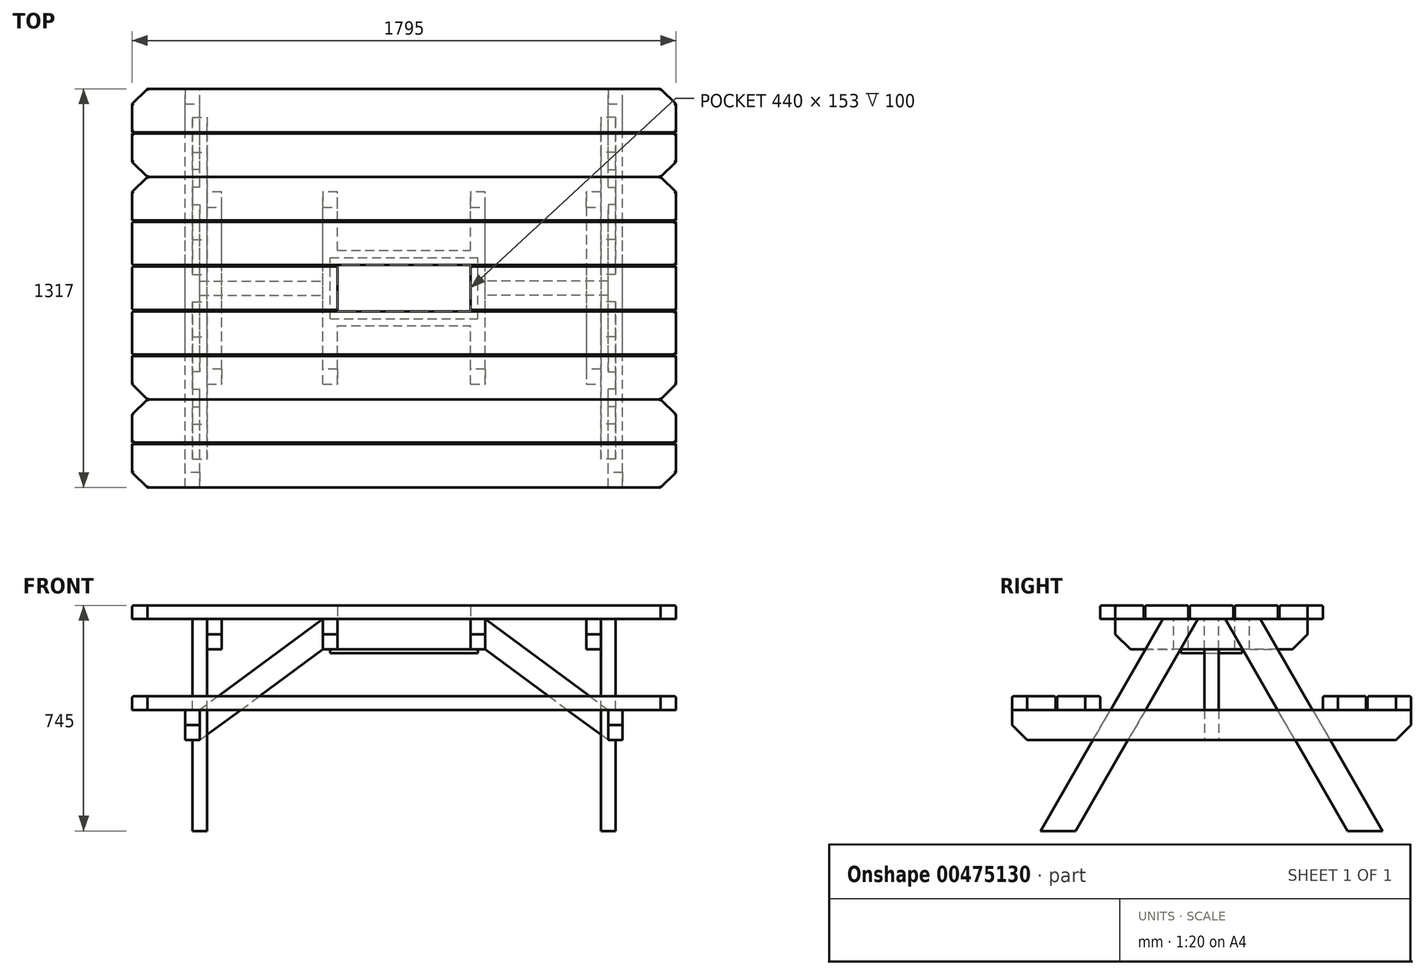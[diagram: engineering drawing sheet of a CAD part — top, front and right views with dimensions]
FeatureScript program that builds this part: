
annotation { "Feature Type Name" : "Feature", "Feature Type Description" : "" }
export const myFeature = defineFeature(function(context is Context, id is Id, definition is map)
    precondition{}
    {
        {
            var Q0;
            Q0=qCreatedBy(makeId("Top.planeOp"),FACE);
            var sketch = newSketch(context, id + "F0", { "sketchPlane" : qUnion([Q0])});
            skLineSegment(sketch, "E0.bottom", {"start": v(897.5, -71.5) * mm, "end": v(-897.5, -71.5) * mm});
            skLineSegment(sketch, "E0.top", {"start": v(897.5, 71.5) * mm, "end": v(-897.5, 71.5) * mm});
            skLineSegment(sketch, "E0.left", {"start": v(897.5, -71.5) * mm, "end": v(897.5, 71.5) * mm});
            skLineSegment(sketch, "E0.right", {"start": v(-897.5, -71.5) * mm, "end": v(-897.5, 71.5) * mm});
            skPoint(sketch, "E0.middle", {"position": v(0, 0) * mm});
            skLineSegment(sketch, "E1.bottom", {"start": v(-897.5, -76.5) * mm, "end": v(897.5, -76.5) * mm});
            skLineSegment(sketch, "E1.top", {"start": v(-897.5, -219.5) * mm, "end": v(897.5, -219.5) * mm});
            skLineSegment(sketch, "E1.left", {"start": v(-897.5, -76.5) * mm, "end": v(-897.5, -219.5) * mm});
            skLineSegment(sketch, "E1.right", {"start": v(897.5, -76.5) * mm, "end": v(897.5, -219.5) * mm});
            skLineSegment(sketch, "E2.bottom", {"start": v(-897.5, -224.5) * mm, "end": v(897.5, -224.5) * mm});
            skLineSegment(sketch, "E2.left", {"start": v(-897.5, -224.5) * mm, "end": v(-897.5, -367.5) * mm});
            skLineSegment(sketch, "E2.right", {"start": v(897.5, -224.5) * mm, "end": v(897.5, -367.5) * mm});
            skLineSegment(sketch, "E3.bottom", {"start": v(-897.5, 76.5) * mm, "end": v(897.5, 76.5) * mm});
            skLineSegment(sketch, "E3.top", {"start": v(-897.5, 219.5) * mm, "end": v(897.5, 219.5) * mm});
            skLineSegment(sketch, "E3.left", {"start": v(-897.5, 76.5) * mm, "end": v(-897.5, 219.5) * mm});
            skLineSegment(sketch, "E3.right", {"start": v(897.5, 76.5) * mm, "end": v(897.5, 219.5) * mm});
            skLineSegment(sketch, "E4.bottom", {"start": v(-897.5, 224.5) * mm, "end": v(897.5, 224.5) * mm});
            skLineSegment(sketch, "E4.top", {"start": v(-897.5, 367.5) * mm, "end": v(897.5, 367.5) * mm});
            skLineSegment(sketch, "E4.left", {"start": v(-897.5, 224.5) * mm, "end": v(-897.5, 367.5) * mm});
            skLineSegment(sketch, "E4.right", {"start": v(897.5, 224.5) * mm, "end": v(897.5, 367.5) * mm});
            skLineSegment(sketch, "E5.bottom", {"start": v(-897.5, -367.5) * mm, "end": v(897.5, -367.5) * mm});
            skSolve(sketch);
        }
        {
            var Q0;
            Q0 = qSketchRegion(id + "F0", true);
            extrude(context, id + "F1", {"entities" : qUnion([Q0]), "depth" : 45 * mm, "offsetDistance" : 25 * mm});
        }
        {
            var Q0;
            Q0=qCreatedBy(makeId("Right.planeOp"),FACE);
            cPlane(context, id + "F2", {"entities" : qUnion([Q0]), "cplaneType" : CPlaneType.OFFSET, "offset" : 650 * mm, "width" : 150 * mm, "height" : 150 * mm});
        }
        {
            var Q0;
            Q0=qCreatedBy(id+"F2.planeOp",FACE);
            var sketch = newSketch(context, id + "F3", { "sketchPlane" : qUnion([Q0])});
            skLineSegment(sketch, "E6", {"start": v(160.47, 0) * mm, "end": v(564.62, -700) * mm});
            skLineSegment(sketch, "E7", {"start": v(564.62, -700) * mm, "end": v(449.15, -700) * mm});
            skLineSegment(sketch, "E8", {"start": v(449.15, -700) * mm, "end": v(45, 0) * mm});
            skLineSegment(sketch, "E9", {"start": v(45, 0) * mm, "end": v(160.47, 0) * mm});
            skLineSegment(sketch, "E10", {"start": v(-45, 0) * mm, "end": v(-449.15, -700) * mm});
            skLineSegment(sketch, "E11", {"start": v(-449.15, -700) * mm, "end": v(-564.62, -700) * mm});
            skLineSegment(sketch, "E12", {"start": v(-564.62, -700) * mm, "end": v(-160.47, 0) * mm});
            skLineSegment(sketch, "E13", {"start": v(-160.47, 0) * mm, "end": v(-45, 0) * mm});
            skLineSegment(sketch, "E14", {"start": v(-449.15, -700) * mm, "end": v(-449.15, -593.82) * mm});
            skSolve(sketch);
        }
        {
            var Q0;
            Q0 = qSketchRegion(id + "F3", true);
            extrude(context, id + "F4", {"entities" : qUnion([Q0]), "depth" : 48 * mm, "offsetDistance" : 25 * mm});
        }
        {
            var Q0;
            Q0=makeQuery(id+"F4.opExtrude","CAP_FACE",FACE,{"disambiguationData":[OSD([sQuery(id+"F3.wireOp",EDGE,"E10"),sQuery(id+"F3.wireOp",EDGE,"E11"),sQuery(id+"F3.wireOp",EDGE,"E12"),sQuery(id+"F3.wireOp",EDGE,"E13")])],"isStart":false});
            var sketch = newSketch(context, id + "F5", { "sketchPlane" : qUnion([Q0])});
            skLineSegment(sketch, "E15.bottom", {"start": v(-658.5, -300) * mm, "end": v(658.5, -300) * mm});
            skLineSegment(sketch, "E15.top", {"start": v(-658.5, -400) * mm, "end": v(658.5, -400) * mm});
            skLineSegment(sketch, "E15.left", {"start": v(-658.5, -300) * mm, "end": v(-658.5, -400) * mm});
            skLineSegment(sketch, "E15.right", {"start": v(658.5, -300) * mm, "end": v(658.5, -400) * mm});
            skLineSegment(sketch, "E16", {"start": v(-658.5, -300) * mm, "end": v(-333.68, -300) * mm});
            skSolve(sketch);
        }
        {
            var Q0;
            Q0 = qSketchRegion(id + "F5", true);
            extrude(context, id + "F6", {"entities" : qUnion([Q0]), "operationType" : NewBodyOperationType.ADD, "depth" : 24 * mm, "offsetDistance" : 25 * mm, "hasSecondDirection" : true, "secondDirectionOppositeDirection" : true, "secondDirectionDepth" : 24 * mm});
        }
        {
            var Q0;
            Q0=makeQuery(id+"F4.opExtrude","SWEPT_BODY",BODY,{"disambiguationData":[OSD([sQuery(id+"F3.wireOp",EDGE,"E6"),sQuery(id+"F3.wireOp",EDGE,"E7"),sQuery(id+"F3.wireOp",EDGE,"E8"),sQuery(id+"F3.wireOp",EDGE,"E9")])]});
            var Q1;
            Q1=qCreatedBy(makeId("Right.planeOp"),FACE);
            mirror(context, id + "F7", {"entities" : qUnion([Q0]), "mirrorPlane" : qUnion([Q1])});
        }
        {
            var Q0;
            Q0=makeQuery(id+"F7.opPattern","COPY",FACE,{"derivedFrom":makeQuery(id+"F6.opExtrude","SWEPT_FACE",FACE,{"disambiguationData":[OSD([sQuery(id+"F5.wireOp",EDGE,"E15.bottom")])]}),"instanceName":"1"});
            var sketch = newSketch(context, id + "F8", { "sketchPlane" : qUnion([Q0])});
            skLineSegment(sketch, "E17.bottom", {"start": v(-897.5, -658.5) * mm, "end": v(897.5, -658.5) * mm});
            skLineSegment(sketch, "E17.top", {"start": v(-897.5, -515.5) * mm, "end": v(897.5, -515.5) * mm});
            skLineSegment(sketch, "E17.left", {"start": v(-897.5, -658.5) * mm, "end": v(-897.5, -515.5) * mm});
            skLineSegment(sketch, "E17.right", {"start": v(897.5, -658.5) * mm, "end": v(897.5, -515.5) * mm});
            skLineSegment(sketch, "E18.bottom", {"start": v(-897.5, -510.5) * mm, "end": v(897.5, -510.5) * mm});
            skLineSegment(sketch, "E18.top", {"start": v(-897.5, -367.5) * mm, "end": v(897.5, -367.5) * mm});
            skLineSegment(sketch, "E18.left", {"start": v(-897.5, -510.5) * mm, "end": v(-897.5, -367.5) * mm});
            skLineSegment(sketch, "E18.right", {"start": v(897.5, -510.5) * mm, "end": v(897.5, -367.5) * mm});
            skLineSegment(sketch, "E19.bottom", {"start": v(897.5, 367.5) * mm, "end": v(-897.5, 367.5) * mm});
            skLineSegment(sketch, "E19.top", {"start": v(897.5, 510.5) * mm, "end": v(-897.5, 510.5) * mm});
            skLineSegment(sketch, "E19.left", {"start": v(897.5, 367.5) * mm, "end": v(897.5, 510.5) * mm});
            skLineSegment(sketch, "E19.right", {"start": v(-897.5, 367.5) * mm, "end": v(-897.5, 510.5) * mm});
            skLineSegment(sketch, "E20.bottom", {"start": v(-897.5, 515.5) * mm, "end": v(897.5, 515.5) * mm});
            skLineSegment(sketch, "E20.top", {"start": v(-897.5, 658.5) * mm, "end": v(897.5, 658.5) * mm});
            skLineSegment(sketch, "E20.left", {"start": v(-897.5, 515.5) * mm, "end": v(-897.5, 658.5) * mm});
            skLineSegment(sketch, "E20.right", {"start": v(897.5, 515.5) * mm, "end": v(897.5, 658.5) * mm});
            skSolve(sketch);
        }
        {
            var Q0;
            Q0 = qSketchRegion(id + "F8", true);
            extrude(context, id + "F9", {"entities" : qUnion([Q0]), "depth" : 45 * mm, "offsetDistance" : 25 * mm});
        }
        {
            var Q0;
            Q0=makeQuery(id+"F6.opExtrude","CAP_FACE",FACE,{"disambiguationData":[OSD([sQuery(id+"F5.wireOp",EDGE,"E15.bottom"),sQuery(id+"F5.wireOp",EDGE,"E15.top"),sQuery(id+"F5.wireOp",EDGE,"E15.left"),sQuery(id+"F5.wireOp",EDGE,"E15.right")])],"isStart":false});
            var sketch = newSketch(context, id + "F10", { "sketchPlane" : qUnion([Q0])});
            skCircle(sketch, "E21", {"center": v(-431.43, -325) * mm, "radius": 5 * mm});
            skCircle(sketch, "E22", {"center": v(-405.45, -375) * mm, "radius": 5 * mm});
            skCircle(sketch, "E23", {"center": v(356.98, -325) * mm, "radius": 5 * mm});
            skCircle(sketch, "E24", {"center": v(474.1, -375) * mm, "radius": 5 * mm});
            skSolve(sketch);
        }
        {
            var Q0;
            Q0=makeQuery(id+"F1.opExtrude","CAP_FACE",FACE,{"disambiguationData":[OSD([sQuery(id+"F0.wireOp",EDGE,"E5.bottom"),sQuery(id+"F0.wireOp",EDGE,"E5.top"),sQuery(id+"F0.wireOp",EDGE,"E5.left"),sQuery(id+"F0.wireOp",EDGE,"E5.right")])],"isStart":true});
            var sketch = newSketch(context, id + "F11", { "sketchPlane" : qUnion([Q0])});
            skLineSegment(sketch, "E25.bottom", {"start": v(-650, 317.5) * mm, "end": v(-602, 317.5) * mm});
            skLineSegment(sketch, "E25.top", {"start": v(-650, -317.5) * mm, "end": v(-602, -317.5) * mm});
            skLineSegment(sketch, "E25.left", {"start": v(-650, 317.5) * mm, "end": v(-650, -317.5) * mm});
            skLineSegment(sketch, "E25.right", {"start": v(-602, 317.5) * mm, "end": v(-602, -317.5) * mm});
            skLineSegment(sketch, "E26.bottom", {"start": v(650, -317.5) * mm, "end": v(602, -317.5) * mm});
            skLineSegment(sketch, "E26.top", {"start": v(650, 317.5) * mm, "end": v(602, 317.5) * mm});
            skLineSegment(sketch, "E26.left", {"start": v(650, -317.5) * mm, "end": v(650, 317.5) * mm});
            skLineSegment(sketch, "E26.right", {"start": v(602, -317.5) * mm, "end": v(602, 317.5) * mm});
            skSolve(sketch);
        }
        {
            var Q0;
            Q0 = qSketchRegion(id + "F11", true);
            extrude(context, id + "F12", {"entities" : qUnion([Q0]), "depth" : 100 * mm, "offsetDistance" : 25 * mm});
        }
        {
            var Q0;
            {var subQ0=sQuery(id+"F3.wireOp",EDGE,"E10");var subQ1=sQuery(id+"F3.wireOp",EDGE,"E13");var subQ2=sQuery(id+"F3.wireOp",EDGE,"E12");Q0=makeQuery(id+"F6.boolean.opBoolean","SPLIT",FACE,{"disambiguationData":[TD([makeQuery(id+"F4.opExtrude","SWEPT_FACE",FACE,{"disambiguationData":[OSD([subQ1])]})])],"derivedFrom":makeQuery(id+"F4.opExtrude","CAP_FACE",FACE,{"disambiguationData":[OSD([subQ0,sQuery(id+"F3.wireOp",EDGE,"E11"),subQ2,subQ1])],"isStart":false})});}
            var sketch = newSketch(context, id + "F13", { "sketchPlane" : qUnion([Q0])});
            skCircle(sketch, "E27", {"center": v(-112.04, -24.63) * mm, "radius": 5 * mm});
            skCircle(sketch, "E28", {"center": v(-236.98, -84.16) * mm, "radius": 5 * mm});
            skCircle(sketch, "E29", {"center": v(97.88, -24.63) * mm, "radius": 5 * mm});
            skCircle(sketch, "E30", {"center": v(207.03, -84.16) * mm, "radius": 5 * mm});
            skSolve(sketch);
        }
        {
            var Q0;
            Q0=makeQuery(id+"F1.opExtrude","CAP_FACE",FACE,{"disambiguationData":[OSD([sQuery(id+"F0.wireOp",EDGE,"E1.bottom"),sQuery(id+"F0.wireOp",EDGE,"E1.top"),sQuery(id+"F0.wireOp",EDGE,"E1.left"),sQuery(id+"F0.wireOp",EDGE,"E1.right")])],"isStart":true});
            var sketch = newSketch(context, id + "F14", { "sketchPlane" : qUnion([Q0])});
            skLineSegment(sketch, "E31.bottom", {"start": v(-268, 317.5) * mm, "end": v(-220, 317.5) * mm});
            skLineSegment(sketch, "E31.top", {"start": v(-268, -317.5) * mm, "end": v(-220, -317.5) * mm});
            skLineSegment(sketch, "E31.left", {"start": v(-268, 317.5) * mm, "end": v(-268, -317.5) * mm});
            skLineSegment(sketch, "E31.right", {"start": v(-220, 317.5) * mm, "end": v(-220, -317.5) * mm});
            skLineSegment(sketch, "E32.bottom", {"start": v(220, 317.5) * mm, "end": v(268, 317.5) * mm});
            skLineSegment(sketch, "E32.top", {"start": v(220, -317.5) * mm, "end": v(268, -317.5) * mm});
            skLineSegment(sketch, "E32.left", {"start": v(220, 317.5) * mm, "end": v(220, -317.5) * mm});
            skLineSegment(sketch, "E32.right", {"start": v(268, 317.5) * mm, "end": v(268, -317.5) * mm});
            skLineSegment(sketch, "E33.bottom", {"start": v(-220, -76.5) * mm, "end": v(220, -76.5) * mm});
            skLineSegment(sketch, "E33.top", {"start": v(-220, -124.5) * mm, "end": v(220, -124.5) * mm});
            skLineSegment(sketch, "E33.left", {"start": v(-220, -76.5) * mm, "end": v(-220, -124.5) * mm});
            skLineSegment(sketch, "E33.right", {"start": v(220, -76.5) * mm, "end": v(220, -124.5) * mm});
            skLineSegment(sketch, "E34.left", {"start": v(-220, 124.5) * mm, "end": v(-220, 76.5) * mm});
            skLineSegment(sketch, "E34.right", {"start": v(220, 124.5) * mm, "end": v(220, 76.5) * mm});
            skLineSegment(sketch, "E35", {"start": v(-220, 76.5) * mm, "end": v(220, 76.5) * mm});
            skLineSegment(sketch, "E36", {"start": v(-220, 124.5) * mm, "end": v(220, 124.5) * mm});
            skSolve(sketch);
        }
        {
            var Q0;
            Q0 = qSketchRegion(id + "F14", true);
            extrude(context, id + "F15", {"entities" : qUnion([Q0]), "depth" : 100 * mm, "offsetDistance" : 25 * mm});
        }
        {
            var Q0;
            Q0=makeQuery(id+"F1.opExtrude","CAP_FACE",FACE,{"disambiguationData":[OSD([sQuery(id+"F0.wireOp",EDGE,"E1.bottom"),sQuery(id+"F0.wireOp",EDGE,"E1.top"),sQuery(id+"F0.wireOp",EDGE,"E1.left"),sQuery(id+"F0.wireOp",EDGE,"E1.right")])],"isStart":true});
            var sketch = newSketch(context, id + "F16", { "sketchPlane" : qUnion([Q0])});
            skLineSegment(sketch, "E37.bottom", {"start": v(220, 76.5) * mm, "end": v(-220, 76.5) * mm});
            skLineSegment(sketch, "E37.top", {"start": v(-220, -76.5) * mm, "end": v(220, -76.5) * mm});
            skLineSegment(sketch, "E37.left", {"start": v(-220, 76.5) * mm, "end": v(-220, -76.5) * mm});
            skLineSegment(sketch, "E37.right", {"start": v(220, 76.5) * mm, "end": v(220, -76.5) * mm});
            skSolve(sketch);
        }
        {
            var Q0;
            Q0 = qSketchRegion(id + "F16", true);
            extrude(context, id + "F17", {"entities" : qUnion([Q0]), "operationType" : NewBodyOperationType.REMOVE, "endBound" : BoundingType.THROUGH_ALL, "oppositeDirection" : true, "depth" : 25 * mm, "offsetDistance" : 25 * mm});
        }
        {
            var Q0;
            Q0=makeQuery(id+"F15.opExtrude","CAP_FACE",FACE,{"disambiguationData":[OSD([sQuery(id+"F14.wireOp",EDGE,"E31.bottom"),sQuery(id+"F14.wireOp",EDGE,"E31.top"),sQuery(id+"F14.wireOp",EDGE,"E31.left"),sQuery(id+"F14.wireOp",EDGE,"E31.right"),sQuery(id+"F14.wireOp",EDGE,"E32.bottom"),sQuery(id+"F14.wireOp",EDGE,"E32.top"),sQuery(id+"F14.wireOp",EDGE,"E32.left"),sQuery(id+"F14.wireOp",EDGE,"E32.right"),sQuery(id+"F14.wireOp",EDGE,"E33.bottom"),sQuery(id+"F14.wireOp",EDGE,"E33.top"),sQuery(id+"F14.wireOp",EDGE,"E35"),sQuery(id+"F14.wireOp",EDGE,"yrt6tq8n-YOMr-yxpr-mFNC-kb3xUqAydBUf")])],"isStart":false});
            var sketch = newSketch(context, id + "F18", { "sketchPlane" : qUnion([Q0])});
            skLineSegment(sketch, "E38.bottom", {"start": v(-244, 100.5) * mm, "end": v(244, 100.5) * mm});
            skLineSegment(sketch, "E38.top", {"start": v(-244, -100.5) * mm, "end": v(244, -100.5) * mm});
            skLineSegment(sketch, "E38.left", {"start": v(-244, 100.5) * mm, "end": v(-244, -100.5) * mm});
            skLineSegment(sketch, "E38.right", {"start": v(244, 100.5) * mm, "end": v(244, -100.5) * mm});
            skSolve(sketch);
        }
        {
            var Q0;
            Q0 = qSketchRegion(id + "F18", true);
            extrude(context, id + "F19", {"entities" : qUnion([Q0]), "operationType" : NewBodyOperationType.ADD, "depth" : 12.5 * mm, "offsetDistance" : 25 * mm});
        }
        {
            var Q0;
            Q0=qCreatedBy(makeId("Front.planeOp"),FACE);
            var sketch = newSketch(context, id + "F20", { "sketchPlane" : qUnion([Q0])});
            skLineSegment(sketch, "E39", {"start": v(-674, -400) * mm, "end": v(-268, -100) * mm});
            skLineSegment(sketch, "E40", {"start": v(-268, -100) * mm, "end": v(-268, 0) * mm});
            skLineSegment(sketch, "E41", {"start": v(-268, 0) * mm, "end": v(-674, -300) * mm});
            skLineSegment(sketch, "E42", {"start": v(-674, -300) * mm, "end": v(-674, -400) * mm});
            skSolve(sketch);
        }
        {
            var Q0;
            Q0 = qSketchRegion(id + "F20", true);
            extrude(context, id + "F21", {"entities" : qUnion([Q0]), "depth" : 24 * mm, "offsetDistance" : 25 * mm, "hasSecondDirection" : true, "secondDirectionOppositeDirection" : true, "secondDirectionDepth" : 24 * mm});
        }
        {
            var Q0;
            Q0=makeQuery(id+"F21.opExtrude","SWEPT_BODY",BODY,{"disambiguationData":[OSD([sQuery(id+"F20.wireOp",EDGE,"E39"),sQuery(id+"F20.wireOp",EDGE,"E40"),sQuery(id+"F20.wireOp",EDGE,"E41"),sQuery(id+"F20.wireOp",EDGE,"E42")])]});
            var Q1;
            Q1=qCreatedBy(makeId("Right.planeOp"),FACE);
            mirror(context, id + "F22", {"entities" : qUnion([Q0]), "mirrorPlane" : qUnion([Q1])});
        }
        {
            var Q0;
            Q0=makeQuery(id+"F9.opExtrude","SWEPT_EDGE",EDGE,{"disambiguationData":[OSD([sQuery(id+"F8.wireOp",EDGE,"E17.bottom"),sQuery(id+"F8.wireOp",EDGE,"E17.right")])]});
            var Q1;
            Q1=makeQuery(id+"F9.opExtrude","SWEPT_EDGE",EDGE,{"disambiguationData":[OSD([sQuery(id+"F8.wireOp",EDGE,"E20.top"),sQuery(id+"F8.wireOp",EDGE,"E20.right")])]});
            var Q2;
            Q2=makeQuery(id+"F9.opExtrude","SWEPT_EDGE",EDGE,{"disambiguationData":[OSD([sQuery(id+"F8.wireOp",EDGE,"E20.top"),sQuery(id+"F8.wireOp",EDGE,"E20.left")])]});
            var Q3;
            Q3=makeQuery(id+"F9.opExtrude","SWEPT_EDGE",EDGE,{"disambiguationData":[OSD([sQuery(id+"F8.wireOp",EDGE,"E17.bottom"),sQuery(id+"F8.wireOp",EDGE,"E17.left")])]});
            var Q4;
            Q4=makeQuery(id+"F7.opPattern","COPY",EDGE,{"derivedFrom":makeQuery(id+"F6.opExtrude","SWEPT_EDGE",EDGE,{"disambiguationData":[OSD([sQuery(id+"F5.wireOp",EDGE,"E15.top"),sQuery(id+"F5.wireOp",EDGE,"E15.left")])]}),"instanceName":"1"});
            var Q5;
            Q5=makeQuery(id+"F12.opExtrude","CAP_EDGE",EDGE,{"disambiguationData":[OSD([sQuery(id+"F11.wireOp",EDGE,"E25.top")])],"isStart":false});
            var Q6;
            Q6=makeQuery(id+"F15.opExtrude","CAP_EDGE",EDGE,{"disambiguationData":[OSD([sQuery(id+"F14.wireOp",EDGE,"E31.top")])],"isStart":false});
            var Q7;
            Q7=makeQuery(id+"F15.opExtrude","CAP_EDGE",EDGE,{"disambiguationData":[OSD([sQuery(id+"F14.wireOp",EDGE,"E32.top")])],"isStart":false});
            var Q8;
            Q8=makeQuery(id+"F12.opExtrude","CAP_EDGE",EDGE,{"disambiguationData":[OSD([sQuery(id+"F11.wireOp",EDGE,"E26.bottom")])],"isStart":false});
            var Q9;
            Q9=makeQuery(id+"F15.opExtrude","CAP_EDGE",EDGE,{"disambiguationData":[OSD([sQuery(id+"F14.wireOp",EDGE,"E31.bottom")])],"isStart":false});
            var Q10;
            Q10=makeQuery(id+"F12.opExtrude","CAP_EDGE",EDGE,{"disambiguationData":[OSD([sQuery(id+"F11.wireOp",EDGE,"E25.bottom")])],"isStart":false});
            var Q11;
            Q11=makeQuery(id+"F15.opExtrude","CAP_EDGE",EDGE,{"disambiguationData":[OSD([sQuery(id+"F14.wireOp",EDGE,"E32.bottom")])],"isStart":false});
            var Q12;
            Q12=makeQuery(id+"F12.opExtrude","CAP_EDGE",EDGE,{"disambiguationData":[OSD([sQuery(id+"F11.wireOp",EDGE,"E26.top")])],"isStart":false});
            var Q13;
            Q13=makeQuery(id+"F6.opExtrude","SWEPT_EDGE",EDGE,{"disambiguationData":[OSD([sQuery(id+"F5.wireOp",EDGE,"E15.top"),sQuery(id+"F5.wireOp",EDGE,"E15.left")])]});
            var Q14;
            Q14=makeQuery(id+"F7.opPattern","COPY",EDGE,{"derivedFrom":makeQuery(id+"F6.opExtrude","SWEPT_EDGE",EDGE,{"disambiguationData":[OSD([sQuery(id+"F5.wireOp",EDGE,"E15.top"),sQuery(id+"F5.wireOp",EDGE,"E15.right")])]}),"instanceName":"1"});
            var Q15;
            Q15=makeQuery(id+"F6.opExtrude","SWEPT_EDGE",EDGE,{"disambiguationData":[OSD([sQuery(id+"F5.wireOp",EDGE,"E15.top"),sQuery(id+"F5.wireOp",EDGE,"E15.right")])]});
            var Q16;
            Q16=makeQuery(id+"F1.opExtrude","SWEPT_EDGE",EDGE,{"disambiguationData":[OSD([sQuery(id+"F0.wireOp",EDGE,"E4.top"),sQuery(id+"F0.wireOp",EDGE,"E4.left")])]});
            var Q17;
            Q17=makeQuery(id+"F1.opExtrude","SWEPT_EDGE",EDGE,{"disambiguationData":[OSD([sQuery(id+"F0.wireOp",EDGE,"E2.left"),sQuery(id+"F0.wireOp",EDGE,"E5.bottom")])]});
            var Q18;
            Q18=makeQuery(id+"F1.opExtrude","SWEPT_EDGE",EDGE,{"disambiguationData":[OSD([sQuery(id+"F0.wireOp",EDGE,"E2.right"),sQuery(id+"F0.wireOp",EDGE,"E5.bottom")])]});
            var Q19;
            Q19=makeQuery(id+"F1.opExtrude","SWEPT_EDGE",EDGE,{"disambiguationData":[OSD([sQuery(id+"F0.wireOp",EDGE,"E4.top"),sQuery(id+"F0.wireOp",EDGE,"E4.right")])]});
            var Q20;
            Q20=makeQuery(id+"F9.opExtrude","SWEPT_EDGE",EDGE,{"disambiguationData":[OSD([sQuery(id+"F8.wireOp",EDGE,"E19.bottom"),sQuery(id+"F8.wireOp",EDGE,"E19.left")])]});
            var Q21;
            Q21=makeQuery(id+"F9.opExtrude","SWEPT_EDGE",EDGE,{"disambiguationData":[OSD([sQuery(id+"F8.wireOp",EDGE,"E18.top"),sQuery(id+"F8.wireOp",EDGE,"E18.right")])]});
            var Q22;
            Q22=makeQuery(id+"F9.opExtrude","SWEPT_EDGE",EDGE,{"disambiguationData":[OSD([sQuery(id+"F8.wireOp",EDGE,"E19.bottom"),sQuery(id+"F8.wireOp",EDGE,"E19.right")])]});
            var Q23;
            Q23=makeQuery(id+"F9.opExtrude","SWEPT_EDGE",EDGE,{"disambiguationData":[OSD([sQuery(id+"F8.wireOp",EDGE,"E18.top"),sQuery(id+"F8.wireOp",EDGE,"E18.left")])]});
            chamfer(context, id + "F23", {"entities" : qUnion([Q0, Q1, Q2, Q3, Q4, Q5, Q6, Q7, Q8, Q9, Q10, Q11, Q12, Q13, Q14, Q15, Q16, Q17, Q18, Q19, Q20, Q21, Q22, Q23]), "width" : 50 * mm, "tangentPropagation" : true});
        }
        {
            var Q0;
            Q0=makeQuery(id+"F9.opExtrude","CAP_FACE",FACE,{"disambiguationData":[OSD([sQuery(id+"F8.wireOp",EDGE,"E17.bottom"),sQuery(id+"F8.wireOp",EDGE,"E17.top"),sQuery(id+"F8.wireOp",EDGE,"E17.left"),sQuery(id+"F8.wireOp",EDGE,"E17.right")])],"isStart":false});
            var Q1;
            Q1=makeQuery(id+"F9.opExtrude","CAP_FACE",FACE,{"disambiguationData":[OSD([sQuery(id+"F8.wireOp",EDGE,"E18.bottom"),sQuery(id+"F8.wireOp",EDGE,"E18.top"),sQuery(id+"F8.wireOp",EDGE,"E18.left"),sQuery(id+"F8.wireOp",EDGE,"E18.right")])],"isStart":false});
            var Q2;
            Q2=makeQuery(id+"F1.opExtrude","CAP_FACE",FACE,{"disambiguationData":[OSD([sQuery(id+"F0.wireOp",EDGE,"E2.bottom"),sQuery(id+"F0.wireOp",EDGE,"E2.left"),sQuery(id+"F0.wireOp",EDGE,"E2.right"),sQuery(id+"F0.wireOp",EDGE,"E5.bottom")])],"isStart":false});
            var Q3;
            Q3=makeQuery(id+"F1.opExtrude","CAP_FACE",FACE,{"disambiguationData":[OSD([sQuery(id+"F0.wireOp",EDGE,"E1.bottom"),sQuery(id+"F0.wireOp",EDGE,"E1.top"),sQuery(id+"F0.wireOp",EDGE,"E1.left"),sQuery(id+"F0.wireOp",EDGE,"E1.right")])],"isStart":false});
            var Q4;
            {var subQ0=sQuery(id+"F0.wireOp",EDGE,"E0.bottom");var subQ1=sQuery(id+"F0.wireOp",EDGE,"E0.right");var subQ2=sQuery(id+"F0.wireOp",EDGE,"E0.top");Q4=makeQuery(id+"F17.boolean.opBoolean","SPLIT",FACE,{"disambiguationData":[TD([makeQuery(id+"F1.opExtrude","SWEPT_FACE",FACE,{"disambiguationData":[OSD([subQ1])]})])],"derivedFrom":makeQuery(id+"F1.opExtrude","CAP_FACE",FACE,{"disambiguationData":[OSD([subQ0,subQ2,sQuery(id+"F0.wireOp",EDGE,"E0.left"),subQ1])],"isStart":false})});}
            var Q5;
            {var subQ0=sQuery(id+"F0.wireOp",EDGE,"E0.bottom");var subQ1=sQuery(id+"F0.wireOp",EDGE,"E0.top");var subQ2=sQuery(id+"F0.wireOp",EDGE,"E0.left");Q5=makeQuery(id+"F17.boolean.opBoolean","SPLIT",FACE,{"disambiguationData":[TD([makeQuery(id+"F1.opExtrude","SWEPT_FACE",FACE,{"disambiguationData":[OSD([subQ2])]})])],"derivedFrom":makeQuery(id+"F1.opExtrude","CAP_FACE",FACE,{"disambiguationData":[OSD([subQ0,subQ1,subQ2,sQuery(id+"F0.wireOp",EDGE,"E0.right")])],"isStart":false})});}
            var Q6;
            Q6=makeQuery(id+"F1.opExtrude","CAP_FACE",FACE,{"disambiguationData":[OSD([sQuery(id+"F0.wireOp",EDGE,"E3.bottom"),sQuery(id+"F0.wireOp",EDGE,"E3.top"),sQuery(id+"F0.wireOp",EDGE,"E3.left"),sQuery(id+"F0.wireOp",EDGE,"E3.right")])],"isStart":false});
            var Q7;
            Q7=makeQuery(id+"F1.opExtrude","CAP_FACE",FACE,{"disambiguationData":[OSD([sQuery(id+"F0.wireOp",EDGE,"E4.bottom"),sQuery(id+"F0.wireOp",EDGE,"E4.top"),sQuery(id+"F0.wireOp",EDGE,"E4.left"),sQuery(id+"F0.wireOp",EDGE,"E4.right")])],"isStart":false});
            var Q8;
            Q8=makeQuery(id+"F9.opExtrude","CAP_FACE",FACE,{"disambiguationData":[OSD([sQuery(id+"F8.wireOp",EDGE,"E19.bottom"),sQuery(id+"F8.wireOp",EDGE,"E19.top"),sQuery(id+"F8.wireOp",EDGE,"E19.left"),sQuery(id+"F8.wireOp",EDGE,"E19.right")])],"isStart":false});
            var Q9;
            Q9=makeQuery(id+"F9.opExtrude","CAP_FACE",FACE,{"disambiguationData":[OSD([sQuery(id+"F8.wireOp",EDGE,"E20.bottom"),sQuery(id+"F8.wireOp",EDGE,"E20.top"),sQuery(id+"F8.wireOp",EDGE,"E20.left"),sQuery(id+"F8.wireOp",EDGE,"E20.right")])],"isStart":false});
            var Q10;
            Q10=makeQuery(id+"F1.opExtrude","SWEPT_FACE",FACE,{"disambiguationData":[OSD([sQuery(id+"F0.wireOp",EDGE,"E1.left")])]});
            var Q11;
            Q11=makeQuery(id+"F1.opExtrude","SWEPT_FACE",FACE,{"disambiguationData":[OSD([sQuery(id+"F0.wireOp",EDGE,"E0.right")])]});
            var Q12;
            Q12=makeQuery(id+"F1.opExtrude","SWEPT_FACE",FACE,{"disambiguationData":[OSD([sQuery(id+"F0.wireOp",EDGE,"E3.left")])]});
            fillet(context, id + "F24", {"entities" : qUnion([Q0, Q1, Q2, Q3, Q4, Q5, Q6, Q7, Q8, Q9, Q10, Q11, Q12]), "radius" : 5 * mm, "tangentPropagation" : true, "allowEdgeOverflow" : false});
        }
    });
